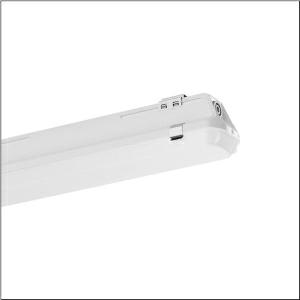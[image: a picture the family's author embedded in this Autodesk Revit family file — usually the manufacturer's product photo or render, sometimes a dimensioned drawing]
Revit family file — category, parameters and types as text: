
# Revit family: monsun_r__11_51fp107p430h_5718
name_source: partatom
category: Lighting Fixtures
units: mm (PartAtom-declared; Revit-internal decimal feet)

## family parameters
Cut with Voids When Loaded = No
Host = Face
Light Source = No
Part Type = Normal
Room Calculation Point = No
Round Connector Dimension = Use Diameter
Shared = No

## types (1)
- Monsun® 11 (1 x LED, 3970 lm, 22.2 W, 4000K)
    Apparent Load = 22 VA
    CIE Flux Codes = 47 77 93 94 100
    Color Rendering = 80
    Color Temperature = 4000K
    Default Elevation = 1800 mm
    Description = Monsun® 11, damp-proof luminaire, chain hanger, primary optical cover: enclosure, of PMMA, light emission: direct distribution, primary light characteristic: symmetric, installation type: suspended mounting, surface-mounted, horizontal mounting, vertical mounting, LED, rated luminous flux: 3.970lm, luminous efficacy: 179lm/W, light colour: 840, colour temperature: 4000K, control gear: ON/OFF, with terminal, 3-pole, max. 2.5mm², mains connection: 220..240V, AC, 50/60Hz, rated input power: 22W, luminaire housing, of glass-fibre reinforced polyester, uncoated, bright grey, incl. chain hanger, length: 1.590mm, width: 90mm, height: 88mm, clip for enclosure, of stainless steel (V2A), ceiling mounting element, of stainless steel (V2A), chain hanger, of stainless steel (V2A), protection rating (complete): IP66, insulation class (complete): insulation class I (protective earthing), certification: CE, ENEC, VDE, UKCA, protection symbol: D, impact resistance: IK04, permissible operating ambient temperature: -35..+40°C, standard: EN 50419, EN 60598-2-1, no direct snow, no direct sun, no direct rain, for indoor or canopied outdoor use, corresponds to IFS (International Featured Standards) requirements for safety and quality in the food industry, contact your sales advisor before using the luminaires in applications with unclear chemical exposure, large temperature fluctuations or condensation-forming humidity, LABS conformity tested according to VDMA 24364:2018-05, packaging unit: 1 piece
    Height = 89 mm
    Lamp = 1 x LED
    Lamp Light Flux = 3970 lm
    Lamp Power = 22.2 W
    Lamp count = 1
    Length = 1590 mm
    Luminous efficacy = 179 lm/W
    Manufacturer = Siteco
    ModVariant = No
    Model = 51FP107P430H
    Mounting Place = Ceiling
    Mounting Type = Surface mounted
    Number of Poles = 1
    OnlyDefault = Yes
    Power Factor = 1
    Product Name = Monsun® 11
    Product group = damp-proof luminaire
    ProductGroupID = 301
    Protection Class = Protection class I
    Protection Degree = IP 66
    RLX_Detail_Level = 1
    RLX_Emergency_Light_Flux = 0 lm
    RLX_Emergency_Type = 0
    RLX_Emergency_Type_DB = No
    RlxData = <blob elided: 88541 chars, md5=de97e2a1>
    Socket = socket
    Standby Power = 0 W
    System Light Flux = 3970 lm
    System Power = 22 W
    Type Comments = Product without accessories
    Type Image = l_1349237.jpg
    URL = http://relux.com
    VarID = ---
    Voltage = 0 V
    Weight = 0.00 kg
    Width = 90 mm

## geometry (parser evidence)
native form markers: Blend x4, Sweep x13
no freeform markers — native parametric forms only
